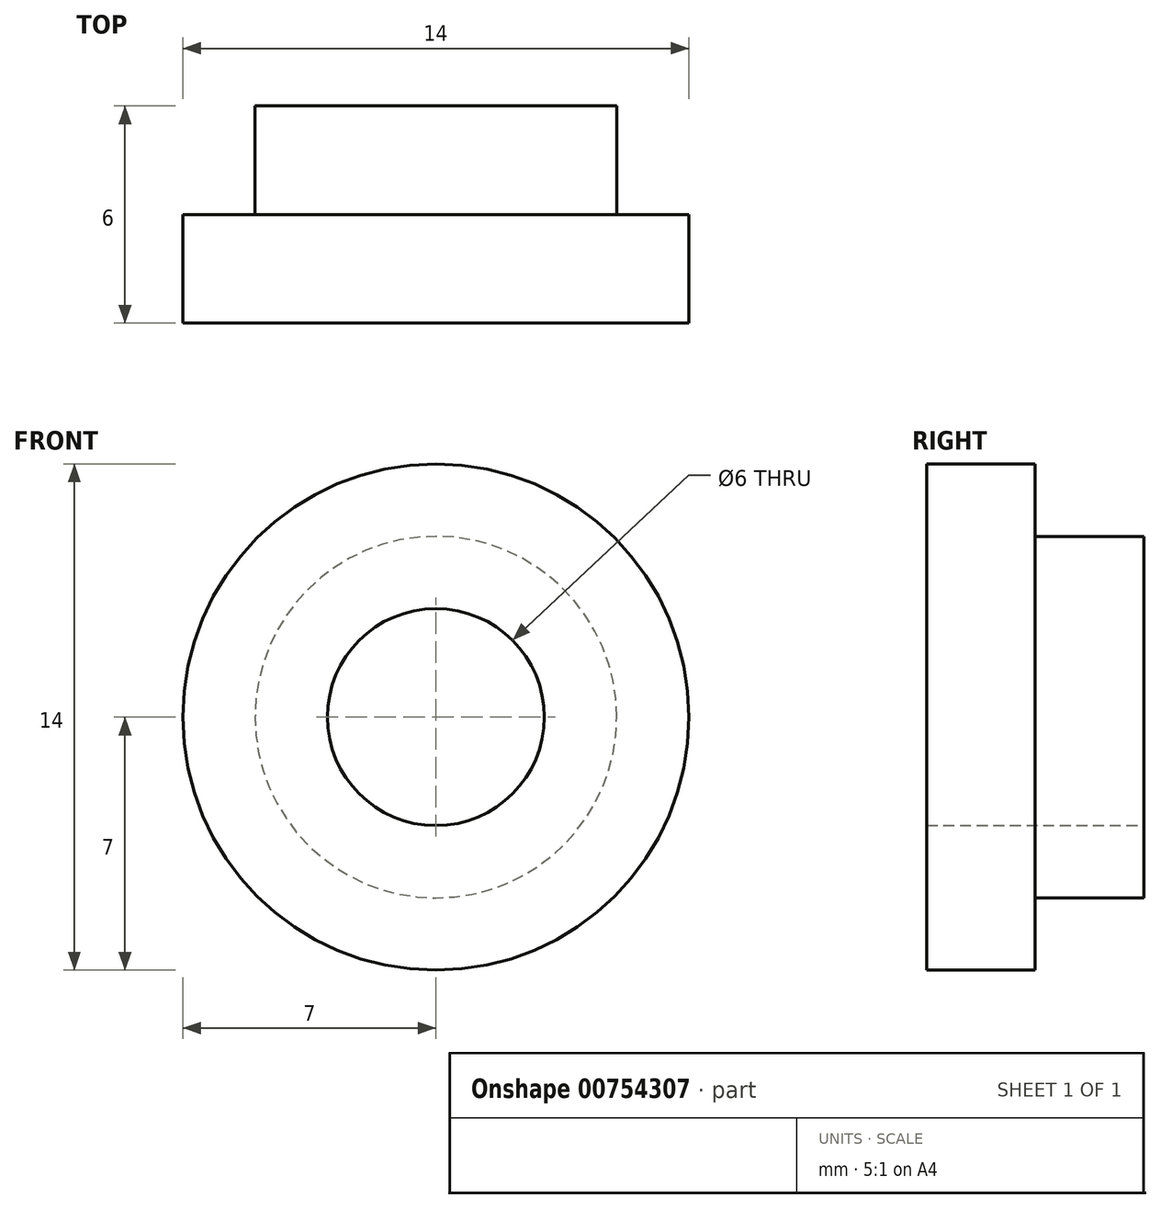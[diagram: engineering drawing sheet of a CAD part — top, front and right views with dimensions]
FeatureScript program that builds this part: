
annotation { "Feature Type Name" : "Feature", "Feature Type Description" : "" }
export const myFeature = defineFeature(function(context is Context, id is Id, definition is map)
    precondition{}
    {
        {
            var Q0;
            Q0=qCreatedBy(makeId("Front.planeOp"),FACE);
            var sketch = newSketch(context, id + "F0", { "sketchPlane" : qUnion([Q0])});
            skCircle(sketch, "E0", {"center": v(0, 0) * mm, "radius": 5 * mm});
            skCircle(sketch, "E1", {"center": v(0, 0) * mm, "radius": 7 * mm});
            skCircle(sketch, "E2", {"center": v(0, 0) * mm, "radius": 3 * mm});
            skSolve(sketch);
        }
        {
            var Q0;
            Q0=makeQuery(id+"F0.imprint","IMPRINT",FACE,{"disambiguationData":[TD([[makeQuery(id+"F0.imprint","IMPRINT",EDGE,{"derivedFrom":sQuery(id+"F0.wireOp",EDGE,"E0")}),-1.0]])]});
            extrude(context, id + "F1", {"entities" : qUnion([Q0]), "depth" : 3 * mm, "offsetDistance" : 25 * mm});
        }
        {
            var Q0;
            Q0=makeQuery(id+"F0.imprint","IMPRINT",FACE,{"disambiguationData":[TD([[makeQuery(id+"F0.imprint","IMPRINT",EDGE,{"derivedFrom":sQuery(id+"F0.wireOp",EDGE,"E0")}),1.0]])]});
            extrude(context, id + "F2", {"entities" : qUnion([Q0]), "operationType" : NewBodyOperationType.ADD, "depth" : 3 * mm, "offsetDistance" : 25 * mm, "hasSecondDirection" : true, "secondDirectionOppositeDirection" : true, "secondDirectionDepth" : 3 * mm});
        }
    });
